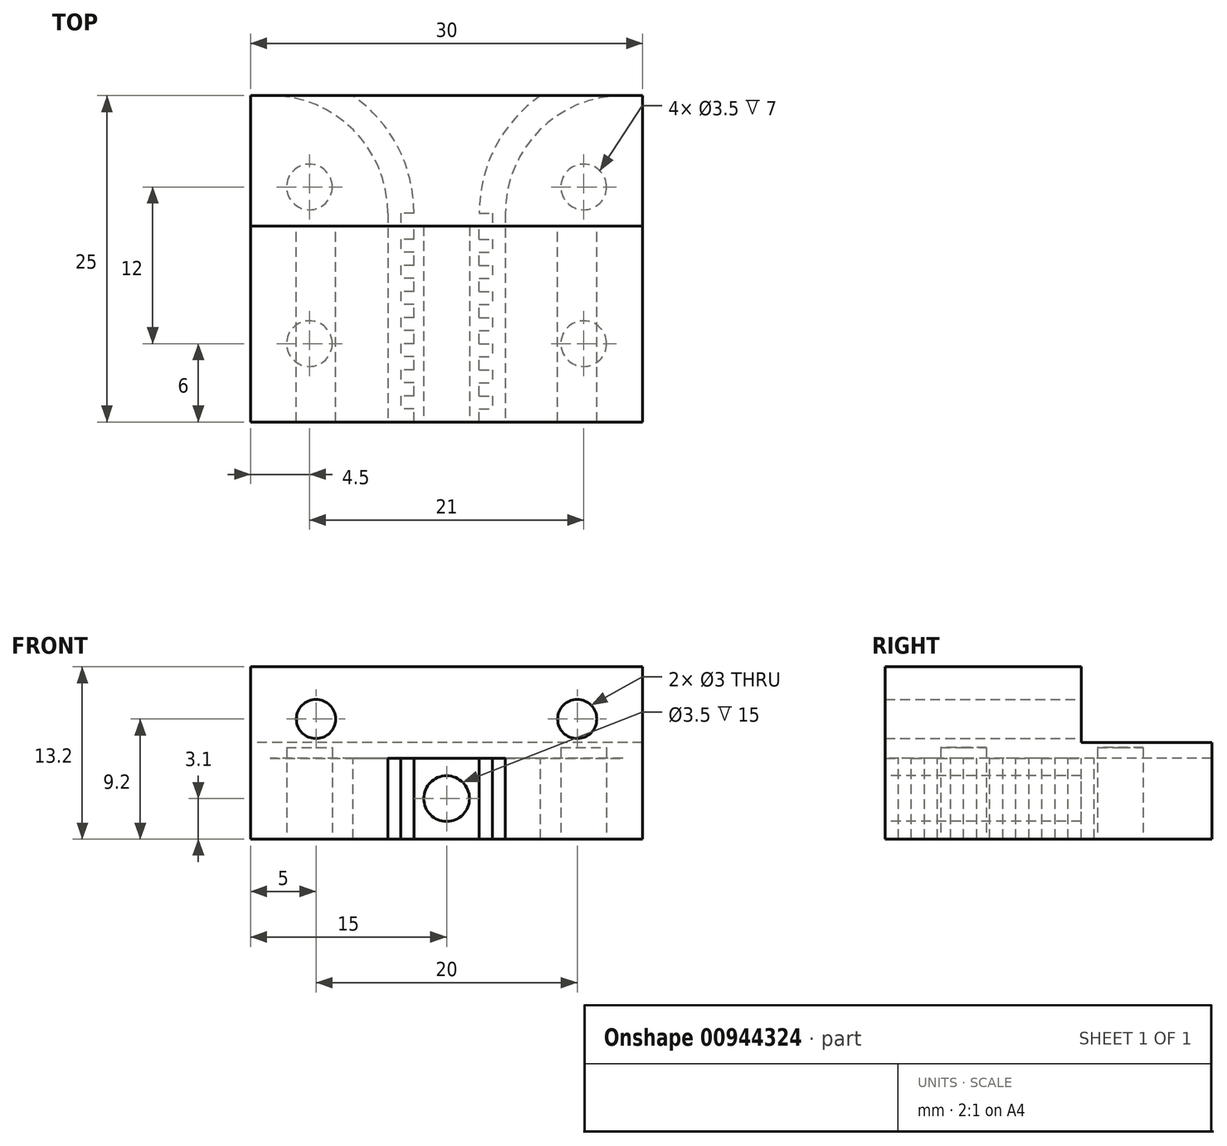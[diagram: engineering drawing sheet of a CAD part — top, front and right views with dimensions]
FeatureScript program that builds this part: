
annotation { "Feature Type Name" : "Feature", "Feature Type Description" : "" }
export const myFeature = defineFeature(function(context is Context, id is Id, definition is map)
    precondition{}
    {
        {
            var Q0;
            Q0=qCreatedBy(makeId("Front.planeOp"),FACE);
            var sketch = newSketch(context, id + "F0", { "sketchPlane" : qUnion([Q0])});
            skLineSegment(sketch, "E0.bottom", {"start": v(15, -3) * mm, "end": v(-15, -3) * mm});
            skLineSegment(sketch, "E0.top", {"start": v(15, 4) * mm, "end": v(-15, 4) * mm});
            skLineSegment(sketch, "E0.left", {"start": v(15, -3) * mm, "end": v(15, 4) * mm});
            skLineSegment(sketch, "E0.right", {"start": v(-15, -3) * mm, "end": v(-15, 4) * mm});
            skPoint(sketch, "E0.middle", {"position": v(0, 0) * mm});
            skCircle(sketch, "E1", {"center": v(-10, 0) * mm, "radius": 1.5 * mm});
            skCircle(sketch, "E2.MirrorC", {"center": v(10, 0) * mm, "radius": 1.5 * mm});
            skSolve(sketch);
        }
        {
            var Q0;
            Q0=makeQuery(id+"F0.imprint","IMPRINT",FACE,{"disambiguationData":[TD([[makeQuery(id+"F0.imprint","IMPRINT",EDGE,{"derivedFrom":sQuery(id+"F0.wireOp",EDGE,"E0.bottom")}),-1.0]])]});
            extrude(context, id + "F1", {"entities" : qUnion([Q0]), "depth" : 25 * mm, "offsetDistance" : 25 * mm});
        }
        {
            var Q0;
            Q0=makeQuery(id+"F1.opExtrude","SWEPT_FACE",FACE,{"disambiguationData":[OSD([sQuery(id+"F0.wireOp",EDGE,"E0.bottom")])]});
            var sketch = newSketch(context, id + "F2", { "sketchPlane" : qUnion([Q0])});
            skArc(sketch, "E3", {"start": v(-13.5, 0) * mm, "mid": v(-7.14, 2.64) * mm, "end": v(-4.5, 9) * mm});
            skLineSegment(sketch, "E4", {"start": v(-4.5, 9) * mm, "end": v(-4.5, 25) * mm});
            skLineSegment(sketch, "E5", {"start": v(-2.5, 25) * mm, "end": v(-2.5, 24) * mm});
            skArc(sketch, "E6", {"start": v(-7.18, 0) * mm, "mid": v(-3.74, 3.93) * mm, "end": v(-2.5, 9) * mm});
            skLineSegment(sketch, "E7", {"start": v(-13.5, 9) * mm, "end": v(4.14, 9) * mm, "construction": true});
            skLineSegment(sketch, "E8.top", {"start": v(-3.5, 23) * mm, "end": v(-3.5, 24) * mm});
            skLineSegment(sketch, "E8.left", {"start": v(-2.5, 23) * mm, "end": v(-3.5, 23) * mm});
            skLineSegment(sketch, "E8.right", {"start": v(-2.5, 24) * mm, "end": v(-3.5, 24) * mm});
            skLineSegment(sketch, "E9.1.0.0", {"start": v(-2.5, 21) * mm, "end": v(-3.5, 21) * mm});
            skLineSegment(sketch, "E9.1.0.1", {"start": v(-3.5, 21) * mm, "end": v(-3.5, 22) * mm});
            skLineSegment(sketch, "E9.1.0.2", {"start": v(-2.5, 23) * mm, "end": v(-2.5, 22) * mm});
            skLineSegment(sketch, "E9.1.0.3", {"start": v(-2.5, 22) * mm, "end": v(-3.5, 22) * mm});
            skLineSegment(sketch, "E9.2.0.0", {"start": v(-2.5, 19) * mm, "end": v(-3.5, 19) * mm});
            skLineSegment(sketch, "E9.2.0.1", {"start": v(-3.5, 19) * mm, "end": v(-3.5, 20) * mm});
            skLineSegment(sketch, "E9.2.0.2", {"start": v(-2.5, 21) * mm, "end": v(-2.5, 20) * mm});
            skLineSegment(sketch, "E9.2.0.3", {"start": v(-2.5, 20) * mm, "end": v(-3.5, 20) * mm});
            skLineSegment(sketch, "E9.3.0.0", {"start": v(-2.5, 17) * mm, "end": v(-3.5, 17) * mm});
            skLineSegment(sketch, "E9.3.0.1", {"start": v(-3.5, 17) * mm, "end": v(-3.5, 18) * mm});
            skLineSegment(sketch, "E9.3.0.2", {"start": v(-2.5, 19) * mm, "end": v(-2.5, 18) * mm});
            skLineSegment(sketch, "E9.3.0.3", {"start": v(-2.5, 18) * mm, "end": v(-3.5, 18) * mm});
            skLineSegment(sketch, "E9.4.0.0", {"start": v(-2.5, 15) * mm, "end": v(-3.5, 15) * mm});
            skLineSegment(sketch, "E9.4.0.1", {"start": v(-3.5, 15) * mm, "end": v(-3.5, 16) * mm});
            skLineSegment(sketch, "E9.4.0.2", {"start": v(-2.5, 17) * mm, "end": v(-2.5, 16) * mm});
            skLineSegment(sketch, "E9.4.0.3", {"start": v(-2.5, 16) * mm, "end": v(-3.5, 16) * mm});
            skLineSegment(sketch, "E9.5.0.0", {"start": v(-2.5, 13) * mm, "end": v(-3.5, 13) * mm});
            skLineSegment(sketch, "E9.5.0.1", {"start": v(-3.5, 13) * mm, "end": v(-3.5, 14) * mm});
            skLineSegment(sketch, "E9.5.0.2", {"start": v(-2.5, 15) * mm, "end": v(-2.5, 14) * mm});
            skLineSegment(sketch, "E9.5.0.3", {"start": v(-2.5, 14) * mm, "end": v(-3.5, 14) * mm});
            skLineSegment(sketch, "E9.6.0.0", {"start": v(-2.5, 11) * mm, "end": v(-3.5, 11) * mm});
            skLineSegment(sketch, "E9.6.0.1", {"start": v(-3.5, 11) * mm, "end": v(-3.5, 12) * mm});
            skLineSegment(sketch, "E9.6.0.2", {"start": v(-2.5, 13) * mm, "end": v(-2.5, 12) * mm});
            skLineSegment(sketch, "E9.6.0.3", {"start": v(-2.5, 12) * mm, "end": v(-3.5, 12) * mm});
            skLineSegment(sketch, "E9.7.0.0", {"start": v(-2.5, 9) * mm, "end": v(-3.5, 9) * mm});
            skLineSegment(sketch, "E9.7.0.1", {"start": v(-3.5, 9) * mm, "end": v(-3.5, 10) * mm});
            skLineSegment(sketch, "E9.7.0.2", {"start": v(-2.5, 11) * mm, "end": v(-2.5, 10) * mm});
            skLineSegment(sketch, "E9.7.0.3", {"start": v(-2.5, 10) * mm, "end": v(-3.5, 10) * mm});
            skLineSegment(sketch, "E9.direction1", {"start": v(-2.5, 23) * mm, "end": v(-2.5, 21) * mm, "construction": true});
            skLineSegment(sketch, "E10", {"start": v(0, 0) * mm, "end": v(0, 25) * mm, "construction": true});
            skLineSegment(sketch, "E11.MirrorCS", {"start": v(2.5, 23) * mm, "end": v(2.5, 22) * mm});
            skLineSegment(sketch, "E12.MirrorCS", {"start": v(2.5, 25) * mm, "end": v(2.5, 24) * mm});
            skLineSegment(sketch, "E13.MirrorCS", {"start": v(2.5, 19) * mm, "end": v(3.5, 19) * mm});
            skLineSegment(sketch, "E14.MirrorCS", {"start": v(2.5, 16) * mm, "end": v(3.5, 16) * mm});
            skLineSegment(sketch, "E15.MirrorCS", {"start": v(2.5, 18) * mm, "end": v(3.5, 18) * mm});
            skLineSegment(sketch, "E16.MirrorCS", {"start": v(2.5, 22) * mm, "end": v(3.5, 22) * mm});
            skLineSegment(sketch, "E17.MirrorCS", {"start": v(2.5, 21) * mm, "end": v(3.5, 21) * mm});
            skLineSegment(sketch, "E18.MirrorCS", {"start": v(3.5, 9) * mm, "end": v(3.5, 10) * mm});
            skLineSegment(sketch, "E19.MirrorCS", {"start": v(2.5, 24) * mm, "end": v(3.5, 24) * mm});
            skLineSegment(sketch, "E20.MirrorCS", {"start": v(2.5, 9) * mm, "end": v(3.5, 9) * mm});
            skLineSegment(sketch, "E21.MirrorCS", {"start": v(2.5, 21) * mm, "end": v(2.5, 20) * mm});
            skLineSegment(sketch, "E22.MirrorCS", {"start": v(3.5, 11) * mm, "end": v(3.5, 12) * mm});
            skLineSegment(sketch, "E23.MirrorCS", {"start": v(2.5, 12) * mm, "end": v(3.5, 12) * mm});
            skLineSegment(sketch, "E24.MirrorCS", {"start": v(2.5, 17) * mm, "end": v(2.5, 16) * mm});
            skLineSegment(sketch, "E25.MirrorCS", {"start": v(2.5, 23) * mm, "end": v(2.5, 21) * mm, "construction": true});
            skLineSegment(sketch, "E26.MirrorCS", {"start": v(2.5, 15) * mm, "end": v(3.5, 15) * mm});
            skLineSegment(sketch, "E27.MirrorCS", {"start": v(3.5, 19) * mm, "end": v(3.5, 20) * mm});
            skLineSegment(sketch, "E28.MirrorCS", {"start": v(3.5, 15) * mm, "end": v(3.5, 16) * mm});
            skLineSegment(sketch, "E29.MirrorCS", {"start": v(2.5, 19) * mm, "end": v(2.5, 18) * mm});
            skLineSegment(sketch, "E30.MirrorCS", {"start": v(3.5, 21) * mm, "end": v(3.5, 22) * mm});
            skLineSegment(sketch, "E31.MirrorCS", {"start": v(2.5, 15) * mm, "end": v(2.5, 14) * mm});
            skLineSegment(sketch, "E32.MirrorCS", {"start": v(3.5, 23) * mm, "end": v(3.5, 24) * mm});
            skLineSegment(sketch, "E33.MirrorCS", {"start": v(2.5, 13) * mm, "end": v(2.5, 12) * mm});
            skLineSegment(sketch, "E34.MirrorCS", {"start": v(2.5, 20) * mm, "end": v(3.5, 20) * mm});
            skLineSegment(sketch, "E35.MirrorCS", {"start": v(2.5, 11) * mm, "end": v(2.5, 10) * mm});
            skLineSegment(sketch, "E36.MirrorCS", {"start": v(2.5, 14) * mm, "end": v(3.5, 14) * mm});
            skLineSegment(sketch, "E37.MirrorCS", {"start": v(3.5, 13) * mm, "end": v(3.5, 14) * mm});
            skLineSegment(sketch, "E38.MirrorCS", {"start": v(2.5, 23) * mm, "end": v(3.5, 23) * mm});
            skLineSegment(sketch, "E39.MirrorCS", {"start": v(2.5, 17) * mm, "end": v(3.5, 17) * mm});
            skLineSegment(sketch, "E40.MirrorCS", {"start": v(2.5, 13) * mm, "end": v(3.5, 13) * mm});
            skLineSegment(sketch, "E41.MirrorCS", {"start": v(3.5, 17) * mm, "end": v(3.5, 18) * mm});
            skLineSegment(sketch, "E42.MirrorCS", {"start": v(2.5, 11) * mm, "end": v(3.5, 11) * mm});
            skLineSegment(sketch, "E43.MirrorCS", {"start": v(2.5, 10) * mm, "end": v(3.5, 10) * mm});
            skArc(sketch, "E44.MirrorCS", {"start": v(7.18, 0) * mm, "mid": v(3.74, 3.93) * mm, "end": v(2.5, 9) * mm});
            skLineSegment(sketch, "E45.MirrorCS", {"start": v(13.5, 9) * mm, "end": v(-4.14, 9) * mm, "construction": true});
            skLineSegment(sketch, "E46.MirrorCS", {"start": v(4.5, 9) * mm, "end": v(4.5, 25) * mm});
            skArc(sketch, "E47.MirrorCS", {"start": v(13.5, 0) * mm, "mid": v(7.14, 2.64) * mm, "end": v(4.5, 9) * mm});
            skLineSegment(sketch, "E48", {"start": v(-4.5, 25) * mm, "end": v(-15, 25) * mm});
            skLineSegment(sketch, "E49", {"start": v(-15, 25) * mm, "end": v(-15, 0) * mm});
            skLineSegment(sketch, "E50", {"start": v(-15, 0) * mm, "end": v(-13.5, 0) * mm});
            skLineSegment(sketch, "E51", {"start": v(-7.18, 0) * mm, "end": v(7.18, 0) * mm});
            skLineSegment(sketch, "E52", {"start": v(13.5, 0) * mm, "end": v(15, 0) * mm});
            skLineSegment(sketch, "E53", {"start": v(15, 0) * mm, "end": v(15, 25) * mm});
            skLineSegment(sketch, "E54", {"start": v(15, 25) * mm, "end": v(4.5, 25) * mm});
            skSolve(sketch);
        }
        {
            var Q0;
            {var subQ1=sQuery(id+"F2.wireOp",EDGE,"E5");Q0=makeQuery(id+"F2.imprint","IMPRINT",FACE,{"disambiguationData":[TD([[makeQuery(id+"F2.imprint","IMPRINT",EDGE,{"derivedFrom":subQ1}),1.0]])]});}
            extrude(context, id + "F3", {"entities" : qUnion([Q0]), "depth" : 6.2 * mm, "offsetDistance" : 25 * mm});
        }
        {
            var Q0;
            Q0=qSketchRegion(id+"F2",true);
            extrude(context, id + "F4", {"entities" : qUnion([Q0]), "operationType" : NewBodyOperationType.ADD, "depth" : 6.2 * mm, "offsetDistance" : 25 * mm});
        }
        {
            var Q0;
            Q0=makeQuery(id+"F3.opExtrude","SWEPT_FACE",FACE,{"disambiguationData":[OSD([sQuery(id+"F0.wireOp",EDGE,"E0.bottom")])]});
            var sketch = newSketch(context, id + "F5", { "sketchPlane" : qUnion([Q0])});
            skLineSegment(sketch, "E55", {"start": v(0, -3) * mm, "end": v(0, -9.2) * mm, "construction": true});
            skLineSegment(sketch, "E56", {"start": v(0, -9.2) * mm, "end": v(-0.2, -9.17) * mm, "construction": true});
            skLineSegment(sketch, "E57", {"start": v(-2.5, -6.1) * mm, "end": v(2.5, -6.1) * mm, "construction": true});
            skCircle(sketch, "E58", {"center": v(0, -6.1) * mm, "radius": 1.75 * mm});
            skSolve(sketch);
        }
        {
            var Q0;
            Q0=makeQuery(id+"F5.imprint","IMPRINT",FACE,{"disambiguationData":[TD([[makeQuery(id+"F5.imprint","IMPRINT",EDGE,{"derivedFrom":sQuery(id+"F5.wireOp",EDGE,"E58")}),1.0]])]});
            extrude(context, id + "F6", {"entities" : qUnion([Q0]), "operationType" : NewBodyOperationType.REMOVE, "oppositeDirection" : true, "depth" : 15 * mm, "offsetDistance" : 25 * mm});
        }
        {
            var Q0;
            Q0=makeQuery(id+"F4.opExtrude","CAP_FACE",FACE,{"disambiguationData":[OSD([sQuery(id+"F2.wireOp",EDGE,"E46.MirrorCS"),sQuery(id+"F2.wireOp",EDGE,"E47.MirrorCS"),sQuery(id+"F2.wireOp",EDGE,"E52"),sQuery(id+"F2.wireOp",EDGE,"E53"),sQuery(id+"F2.wireOp",EDGE,"E54")])],"isStart":false});
            var sketch = newSketch(context, id + "F7", { "sketchPlane" : qUnion([Q0])});
            skLineSegment(sketch, "E59", {"start": v(10.5, 3.36) * mm, "end": v(10.5, 25.43) * mm, "construction": true});
            skCircle(sketch, "E60", {"center": v(10.5, 7) * mm, "radius": 1.75 * mm});
            skCircle(sketch, "E61", {"center": v(10.5, 19) * mm, "radius": 1.75 * mm});
            skCircle(sketch, "E62.MirrorC", {"center": v(-10.5, 7) * mm, "radius": 1.75 * mm});
            skCircle(sketch, "E63.MirrorC", {"center": v(-10.5, 19) * mm, "radius": 1.75 * mm});
            skSolve(sketch);
        }
        {
            var Q0;
            Q0=qSketchRegion(id+"F7",true);
            extrude(context, id + "F8", {"entities" : qUnion([Q0]), "operationType" : NewBodyOperationType.REMOVE, "oppositeDirection" : true, "depth" : 7 * mm, "offsetDistance" : 25 * mm});
        }
        {
            var Q0;
            Q0=makeQuery(id+"F4.boolean.opBoolean","MERGE",FACE,{"derivedFrom":[makeQuery(id+"F1.opExtrude","CAP_FACE",FACE,{"disambiguationData":[OSD([sQuery(id+"F0.wireOp",EDGE,"E0.bottom"),sQuery(id+"F0.wireOp",EDGE,"E0.top"),sQuery(id+"F0.wireOp",EDGE,"E0.left"),sQuery(id+"F0.wireOp",EDGE,"E0.right"),sQuery(id+"F0.wireOp",EDGE,"E1"),sQuery(id+"F0.wireOp",EDGE,"E2.MirrorC")])],"isStart":true}),makeQuery(id+"F4.opExtrude","SWEPT_FACE",FACE,{"disambiguationData":[OSD([sQuery(id+"F2.wireOp",EDGE,"E50")])]}),makeQuery(id+"F4.opExtrude","SWEPT_FACE",FACE,{"disambiguationData":[OSD([sQuery(id+"F2.wireOp",EDGE,"E52")])]})]});
            var sketch = newSketch(context, id + "F9", { "sketchPlane" : qUnion([Q0])});
            skLineSegment(sketch, "E64.bottom", {"start": v(-15, 4) * mm, "end": v(15, 4) * mm});
            skLineSegment(sketch, "E64.top", {"start": v(-15, -1.8) * mm, "end": v(15, -1.8) * mm});
            skLineSegment(sketch, "E64.left", {"start": v(-15, 4) * mm, "end": v(-15, -1.8) * mm});
            skLineSegment(sketch, "E64.right", {"start": v(15, 4) * mm, "end": v(15, -1.8) * mm});
            skSolve(sketch);
        }
        {
            var Q0;
            Q0=makeQuery(id+"F9.imprint","IMPRINT",FACE,{"disambiguationData":[TD([[makeQuery(id+"F9.imprint","IMPRINT",EDGE,{"derivedFrom":sQuery(id+"F9.wireOp",EDGE,"E64.bottom")}),-1.0]])]});
            extrude(context, id + "F10", {"entities" : qUnion([Q0]), "operationType" : NewBodyOperationType.REMOVE, "oppositeDirection" : true, "depth" : 10 * mm, "offsetDistance" : 25 * mm});
        }
    });
